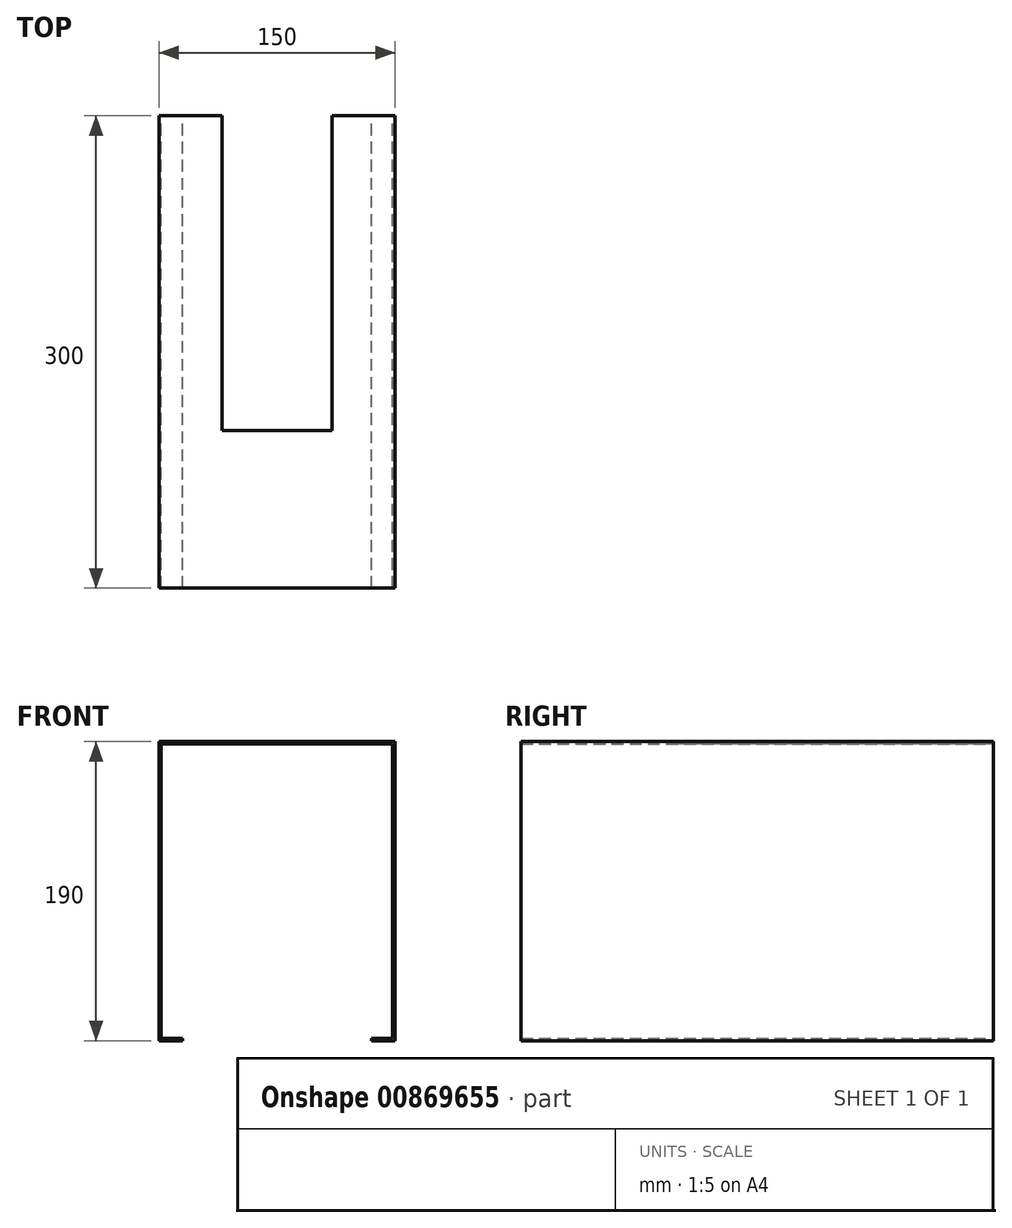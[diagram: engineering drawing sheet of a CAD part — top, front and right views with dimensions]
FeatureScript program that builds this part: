
annotation { "Feature Type Name" : "Feature", "Feature Type Description" : "" }
export const myFeature = defineFeature(function(context is Context, id is Id, definition is map)
    precondition{}
    {
        {
            var Q0;
            Q0=qCreatedBy(makeId("Front.planeOp"),FACE);
            var sketch = newSketch(context, id + "F0", { "sketchPlane" : qUnion([Q0])});
            skLineSegment(sketch, "E0.top", {"start": v(-75, 95) * mm, "end": v(75, 95) * mm});
            skLineSegment(sketch, "E0.left", {"start": v(-75, -95) * mm, "end": v(-75, 95) * mm});
            skLineSegment(sketch, "E0.right", {"start": v(75, -95) * mm, "end": v(75, 95) * mm});
            skLineSegment(sketch, "E1.0", {"start": v(-73.5, -93.5) * mm, "end": v(-73.5, 93.5) * mm});
            skLineSegment(sketch, "E2.0", {"start": v(-73.5, 93.5) * mm, "end": v(73.5, 93.5) * mm});
            skLineSegment(sketch, "E3.0", {"start": v(73.5, -93.5) * mm, "end": v(73.5, 93.5) * mm});
            skLineSegment(sketch, "E4", {"start": v(-75, -95) * mm, "end": v(-60, -95) * mm});
            skLineSegment(sketch, "E5", {"start": v(-60, -95) * mm, "end": v(-60, -93.5) * mm});
            skLineSegment(sketch, "E6", {"start": v(-60, -93.5) * mm, "end": v(-73.5, -93.5) * mm});
            skLineSegment(sketch, "E7.MirrorCS", {"start": v(60, -93.5) * mm, "end": v(73.5, -93.5) * mm});
            skLineSegment(sketch, "E8.MirrorCS", {"start": v(75, -95) * mm, "end": v(60, -95) * mm});
            skLineSegment(sketch, "E9.MirrorCS", {"start": v(60, -95) * mm, "end": v(60, -93.5) * mm});
            skSolve(sketch);
        }
        {
            var Q0;
            Q0 = qSketchRegion(id + "F0", true);
            extrude(context, id + "F1", {"entities" : qUnion([Q0]), "depth" : 300 * mm, "offsetDistance" : 25 * mm});
        }
        {
            var Q0;
            Q0=makeQuery(id+"F1.opExtrude","SWEPT_FACE",FACE,{"disambiguationData":[OSD([sQuery(id+"F0.wireOp",EDGE,"E0.top")])]});
            var sketch = newSketch(context, id + "F2", { "sketchPlane" : qUnion([Q0])});
            skLineSegment(sketch, "E10.bottom", {"start": v(-35, 0) * mm, "end": v(35, 0) * mm});
            skLineSegment(sketch, "E10.top", {"start": v(-35, -200) * mm, "end": v(35, -200) * mm});
            skLineSegment(sketch, "E10.left", {"start": v(-35, 0) * mm, "end": v(-35, -200) * mm});
            skLineSegment(sketch, "E10.right", {"start": v(35, 0) * mm, "end": v(35, -200) * mm});
            skSolve(sketch);
        }
        {
            var Q0;
            Q0 = qSketchRegion(id + "F2", true);
            extrude(context, id + "F3", {"entities" : qUnion([Q0]), "operationType" : NewBodyOperationType.REMOVE, "oppositeDirection" : true, "depth" : 25 * mm, "offsetDistance" : 25 * mm});
        }
    });
